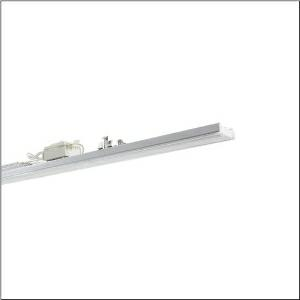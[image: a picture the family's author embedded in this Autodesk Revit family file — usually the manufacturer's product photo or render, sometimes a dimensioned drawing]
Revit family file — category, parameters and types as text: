
# Revit family: licross_r__21_recessed_mo_52tl12dn4axg_5465
name_source: partatom
category: Lighting Fixtures
units: mm (PartAtom-declared; Revit-internal decimal feet)

## family parameters
Cut with Voids When Loaded = No
Host = Face
Light Source = No
Part Type = Normal
Room Calculation Point = No
Round Connector Dimension = Use Diameter
Shared = No

## types (1)
- --- (1 x LED, 10280 lm, 58 W, 4000K)
    Apparent Load = 58 VA
    CIE Flux Codes = 72 92 99 100 100
    Color Rendering = 80
    Color Temperature = 4000K
    Default Elevation = 1800 mm
    Description = Licross® 21 Recessed MO, luminaire insert, of sheet steel, galvanised, coil coated, white, length: 1.500mm, width: 66mm, height: 67mm, LED rated luminous flux: 10.280lm, light colour: 840, control gear: DALI 2, with plug, 5-pole, with phase selection, mains connection: 220..240V, AC, 50/60Hz, rated input power: 58W, internal wiring halogen-free, primary optical cover: cover, of PMMA, light emission: direct distribution, primary light characteristic: symmetric, protection rating (complete): IP40, insulation class (complete): insulation class I (protective earthing), certification: CE, ENEC, VDE, UKCA, protection symbol: D if used in an environment without relevant dust loads with corresponding accessories, impact resistance: IK06, permissible ambient temperature for indoor applications: -25..+35°C, corresponds to IFS (International Featured Standards) requirements for safety and quality in the food industry, reducing of maximum allowable ambient temperature of 5°C with ceiling mounting, LABS conformity tested according to VDMA 24364:2018-05, packaging unit: 1 piece
    Height = 58 mm
    Lamp = 1 x LED
    Lamp Light Flux = 10280 lm
    Lamp Power = 58 W
    Lamp count = 1
    Length = 1500 mm
    Luminous efficacy = 177 lm/W
    Manufacturer = Siteco
    ModVariant = No
    Model = 52TL12DN4AXG
    Mounting Place = Ceiling
    Mounting Type = Pendant
    Number of Poles = 1
    OnlyDefault = Yes
    Power Factor = 1
    Product Name = Licross® 21 Recessed MO
    Product group = luminaire insert | ceiling pendant
    ProductGroupID = 902
    Protection Class = Protection class I
    Protection Degree = IP 40
    RLX_Detail_Level = 1
    RLX_Emergency_Light_Flux = 0 lm
    RLX_Emergency_Type = 0
    RLX_Emergency_Type_DB = No
    RlxData = <blob elided: 24689 chars, md5=2cbae1ef>
    Socket = socket
    Standby Power = 0 W
    System Light Flux = 10280 lm
    System Power = 58 W
    Type Comments = factory setting: luminous flux: 100 % | dim-lin: 254 | 390 mA
    Type Image = l_1296930.jpg
    URL = http://relux.com
    VarID = @adj_147849
    Voltage = 0 V
    Weight = 0.00 kg
    Width = 66 mm

## geometry (parser evidence)
native form markers: Blend x4, Sweep x9
no freeform markers — native parametric forms only
